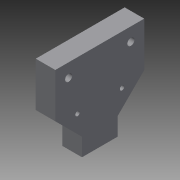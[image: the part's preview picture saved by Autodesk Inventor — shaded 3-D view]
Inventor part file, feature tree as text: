
AUTODESK INVENTOR PART (.ipt)
format: ipt  version: 2013 (Build 170138000, 138)  size: 178,176 bytes
history: native  units: mm
features: sketch x6, extrude x4, hole x2, other x1, pattern_circular x1
ambient origin geometry x8: Origin, YZ Plane, XZ Plane, XY Plane, X Axis, Y Axis, Z Axis, Center Point
feature tree (14):
  other  "ソリッド1"
  extrude  "押し出し1"  Depth=100.0mm
  extrude  "押し出し2"  Depth=100.0mm
  extrude  "押し出し5"  Depth=50.0mm
  hole  "穴1"  [1 undecoded]
  pattern_circular  "円形状パターン2"  [2 undecoded]
  hole  "穴2"  [1 undecoded]
  extrude  "押し出し6"  TaperAngle=135.0deg  [1 undecoded]
  sketch  "スケッチ1"
  sketch  "スケッチ2"
  sketch  "スケッチ3"
  sketch  "スケッチ4"
  sketch  "スケッチ5"
  sketch  "スケッチ6"
note: 5 required parameter values undecoded (feature->parameter linkage not recoverable at this tier; creation-order binding heuristic only, values carry confidence <= 0.55)
